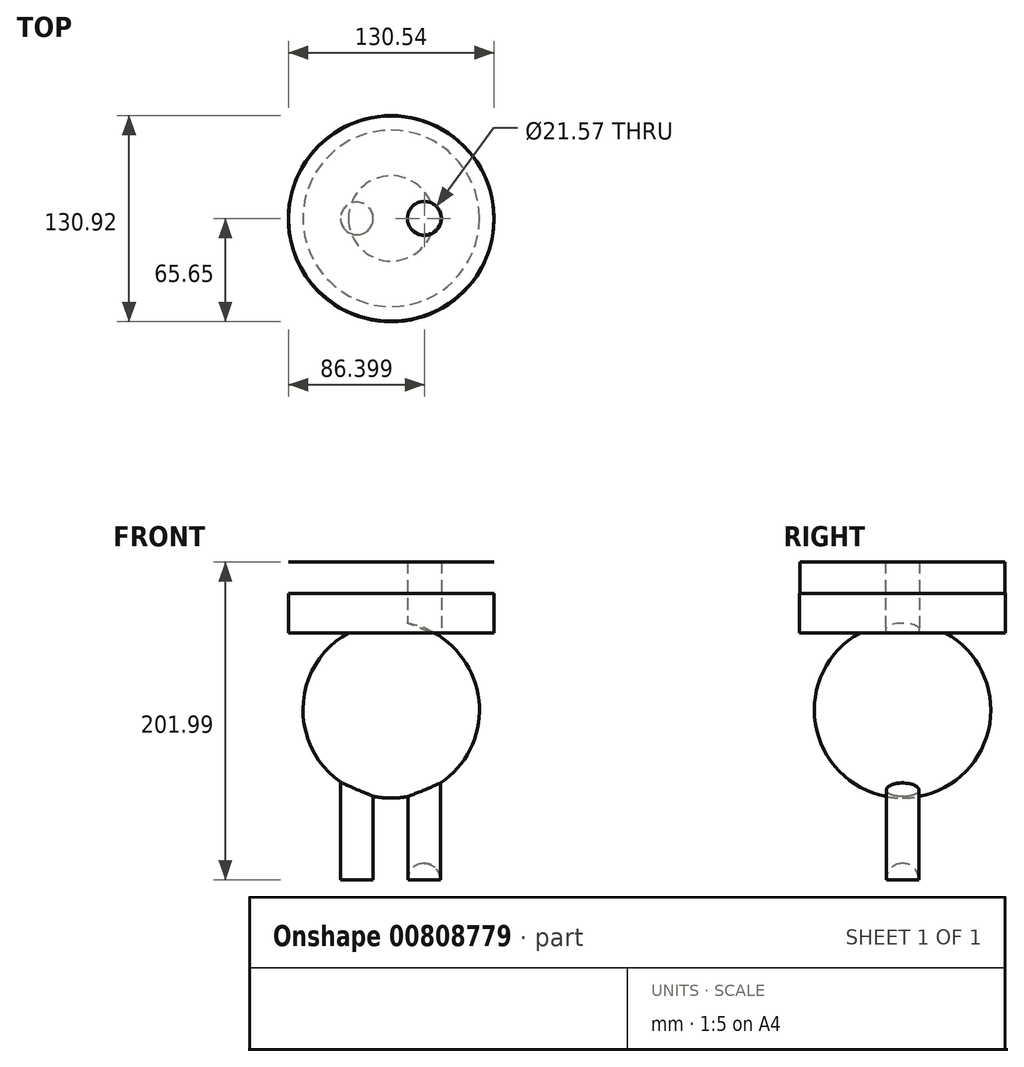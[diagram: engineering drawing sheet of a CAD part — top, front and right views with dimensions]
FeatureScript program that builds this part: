
annotation { "Feature Type Name" : "Feature", "Feature Type Description" : "" }
export const myFeature = defineFeature(function(context is Context, id is Id, definition is map)
    precondition{}
    {
        {
            var Q0;
            Q0=qCreatedBy(makeId("Top.planeOp"),FACE);
            var sketch = newSketch(context, id + "F0", { "sketchPlane" : qUnion([Q0])});
            skCircle(sketch, "E0", {"center": v(0, 0) * mm, "radius": 65.27 * mm});
            skCircle(sketch, "E1.MirrorC", {"center": v(21.13, 0) * mm, "radius": 10.79 * mm});
            skCircle(sketch, "E2", {"center": v(0, -0.37) * mm, "radius": 65.27 * mm});
            skCircle(sketch, "E3.MirrorC", {"center": v(-21.13, 0) * mm, "radius": 10.79 * mm});
            skSolve(sketch);
        }
        {
            var Q0;
            Q0=qCreatedBy(makeId("Front.planeOp"),FACE);
            var sketch = newSketch(context, id + "F1", { "sketchPlane" : qUnion([Q0])});
            skCircle(sketch, "E4", {"center": v(0, -49.03) * mm, "radius": 56.03 * mm});
            skLineSegment(sketch, "E5", {"start": v(0, 7) * mm, "end": v(0, -105.06) * mm});
            skSolve(sketch);
        }
        {
            var Q0;
            {var subQ0=sQuery(id+"F1.wireOp",EDGE,"E5");var subQ1=sQuery(id+"F1.wireOp",EDGE,"E4");var subQ2=makeQuery(id+"F1.imprint","INTERSECT",VERTEX,{"disambiguationData":[OD(0.0)],"derivedFrom":[subQ1,subQ0]});Q0=makeQuery(id+"F1.imprint","IMPRINT",FACE,{"disambiguationData":[TD([[makeQuery(id+"F1.imprint","IMPRINT",EDGE,{"disambiguationData":[TD([[subQ2,1.0]])],"derivedFrom":subQ1}),1.0]])]});}
            var Q1;
            Q1=sQuery(id+"F1.wireOp",EDGE,"E5");
            revolve(context, id + "F2", {"surfaceOperationType" : NewSurfaceOperationType.NEW, "entities" : qUnion([Q0]), "axis" : qUnion([Q1]), "revolveType" : RevolveType.FULL});
        }
        {
            var Q0;
            Q0=qCreatedBy(makeId("Front.planeOp"),FACE);
            var sketch = newSketch(context, id + "F3", { "sketchPlane" : qUnion([Q0])});
            skLineSegment(sketch, "E6.bottom", {"start": v(-32.16, -156.99) * mm, "end": v(-11.45, -156.99) * mm});
            skLineSegment(sketch, "E6.top", {"start": v(-32.16, -87.4) * mm, "end": v(-11.45, -87.4) * mm});
            skLineSegment(sketch, "E6.left", {"start": v(-32.16, -156.99) * mm, "end": v(-32.16, -87.4) * mm});
            skLineSegment(sketch, "E6.right", {"start": v(-11.45, -156.99) * mm, "end": v(-11.45, -87.4) * mm});
            skCircle(sketch, "E7", {"center": v(-21.8, -156.99) * mm, "radius": 10.35 * mm});
            skLineSegment(sketch, "E8.MirrorCS", {"start": v(11.45, -156.99) * mm, "end": v(11.45, -87.4) * mm});
            skLineSegment(sketch, "E9.MirrorCS", {"start": v(32.16, -87.4) * mm, "end": v(11.45, -87.4) * mm});
            skLineSegment(sketch, "E10.MirrorCS", {"start": v(32.16, -156.99) * mm, "end": v(32.16, -87.4) * mm});
            skCircle(sketch, "E11.MirrorC", {"center": v(21.8, -156.99) * mm, "radius": 10.35 * mm});
            skLineSegment(sketch, "E12", {"start": v(-21.8, -167.34) * mm, "end": v(-21.8, -87.4) * mm});
            skLineSegment(sketch, "E13.MirrorCS", {"start": v(21.8, -167.34) * mm, "end": v(21.8, -87.4) * mm});
            skSolve(sketch);
        }
        {
            var Q0;
            {var subQ0=sQuery(id+"F3.wireOp",EDGE,"E7");var subQ3=sQuery(id+"F3.wireOp",EDGE,"E12");var subQ5=makeQuery(id+"F3.imprint","INTERSECT",VERTEX,{"disambiguationData":[OD(0.0)],"derivedFrom":[subQ0,subQ3]});Q0=makeQuery(id+"F3.imprint","IMPRINT",FACE,{"disambiguationData":[TD([[makeQuery(id+"F3.imprint","IMPRINT",EDGE,{"disambiguationData":[TD([[subQ5,-1.0]])],"derivedFrom":subQ3}),1.0]])]});}
            var Q1;
            {var subQ0=sQuery(id+"F3.wireOp",EDGE,"E6.left");Q1=makeQuery(id+"F3.imprint","IMPRINT",FACE,{"disambiguationData":[TD([[makeQuery(id+"F3.imprint","IMPRINT",EDGE,{"derivedFrom":subQ0}),-1.0]])]});}
            var Q2;
            {var subQ1=sQuery(id+"F3.wireOp",EDGE,"E6.bottom");var subQ3=sQuery(id+"F3.wireOp",EDGE,"E12");var subQ4=makeQuery(id+"F3.imprint","INTERSECT",VERTEX,{"derivedFrom":[subQ1,subQ3]});Q2=makeQuery(id+"F3.imprint","IMPRINT",FACE,{"disambiguationData":[TD([[makeQuery(id+"F3.imprint","IMPRINT",EDGE,{"disambiguationData":[TD([[subQ4,-1.0]])],"derivedFrom":subQ3}),1.0]])]});}
            var Q3;
            Q3=sQuery(id+"F3.wireOp",EDGE,"E12");
            revolve(context, id + "F4", {"operationType" : NewBodyOperationType.ADD, "surfaceOperationType" : NewSurfaceOperationType.NEW, "entities" : qUnion([Q0, Q1, Q2]), "axis" : qUnion([Q3]), "revolveType" : RevolveType.FULL});
        }
        {
            var Q0;
            Q0=qCreatedBy(makeId("Front.planeOp"),FACE);
            var sketch = newSketch(context, id + "F5", { "sketchPlane" : qUnion([Q0])});
            skLineSegment(sketch, "E14.MirrorCS", {"start": v(10.57, -156.86) * mm, "end": v(10.57, -87.26) * mm});
            skLineSegment(sketch, "E15.MirrorCS", {"start": v(31.28, -87.26) * mm, "end": v(10.57, -87.26) * mm});
            skLineSegment(sketch, "E16.MirrorCS", {"start": v(31.28, -156.86) * mm, "end": v(31.28, -87.26) * mm});
            skCircle(sketch, "E17.MirrorC", {"center": v(20.93, -156.86) * mm, "radius": 10.35 * mm});
            skLineSegment(sketch, "E18.MirrorCS", {"start": v(20.93, -167.21) * mm, "end": v(20.93, -87.26) * mm});
            skSolve(sketch);
        }
        {
            var Q0;
            {var subQ0=sQuery(id+"F5.wireOp",EDGE,"E17.MirrorC");var subQ1=makeQuery(id+"F5.imprint","INTERSECT",VERTEX,{"derivedFrom":[sQuery(id+"F5.wireOp",EDGE,"E16.MirrorCS"),subQ0]});Q0=makeQuery(id+"F5.imprint","IMPRINT",FACE,{"disambiguationData":[TD([[makeQuery(id+"F5.imprint","IMPRINT",EDGE,{"disambiguationData":[TD([[subQ1,1.0]])],"derivedFrom":subQ0}),-1.0]])]});}
            var Q1;
            {var subQ0=sQuery(id+"F5.wireOp",EDGE,"E16.MirrorCS");Q1=makeQuery(id+"F5.imprint","IMPRINT",FACE,{"disambiguationData":[TD([[makeQuery(id+"F5.imprint","IMPRINT",EDGE,{"derivedFrom":subQ0}),1.0]])]});}
            var Q2;
            Q2=sQuery(id+"F5.wireOp",EDGE,"E18.MirrorCS");
            revolve(context, id + "F6", {"operationType" : NewBodyOperationType.ADD, "surfaceOperationType" : NewSurfaceOperationType.NEW, "entities" : qUnion([Q0, Q1]), "axis" : qUnion([Q2]), "revolveType" : RevolveType.FULL});
        }
        {
            var Q0;
            Q0=makeQuery(id+"F0.imprint","IMPRINT",FACE,{"disambiguationData":[TD([[makeQuery(id+"F0.imprint","IMPRINT",EDGE,{"derivedFrom":sQuery(id+"F0.wireOp",EDGE,"E3.MirrorC")}),1.0]])]});
            var Q1;
            Q1=makeQuery(id+"F0.imprint","IMPRINT",FACE,{"disambiguationData":[TD([[makeQuery(id+"F0.imprint","IMPRINT",EDGE,{"derivedFrom":sQuery(id+"F0.wireOp",EDGE,"E1.MirrorC")}),-1.0]])]});
            extrude(context, id + "F7", {"entities" : qUnion([Q0, Q1]), "operationType" : NewBodyOperationType.ADD, "depth" : 45 * mm, "offsetDistance" : 25 * mm});
        }
        {
            var Q0;
            Q0 = qSketchRegion(id + "F0", true);
            extrude(context, id + "F8", {"entities" : qUnion([Q0]), "operationType" : NewBodyOperationType.ADD, "depth" : 25 * mm, "offsetDistance" : 25 * mm});
        }
    });
